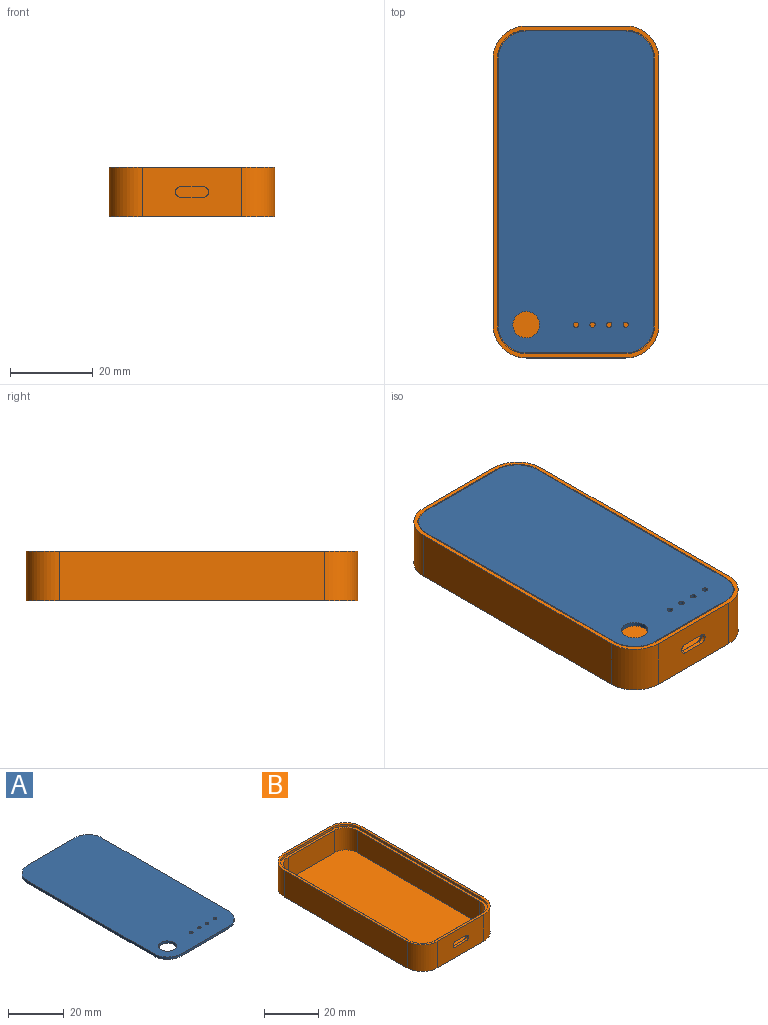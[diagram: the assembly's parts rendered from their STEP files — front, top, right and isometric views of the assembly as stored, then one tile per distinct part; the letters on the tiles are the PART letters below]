
ASSEMBLY  parts=2 mates=1
PART A: 15 faces, bbox 37.6x77.6x1 mm
  f0: plane 24x1mm, normal (0,-1,0), area 24mm2, adj f4,f5,f6,f9
  f1: plane 64x1mm, normal (1,0,0), area 64mm2, adj f4,f5,f6,f7
  f2: plane 24x1mm, normal (0,1,0), area 24mm2, adj f4,f5,f7,f8
  f3: plane 64x1mm, normal (-1,0,0), area 64mm2, adj f4,f5,f8,f9
  f4: plane 77.6x37.6mm, normal (0,0,1), area 2840.6mm2, adj f0,f1,f2,f3,f6,f7,f8,f9
  f5: plane 77.6x37.6mm, normal (0,0,-1), area 2840.6mm2, adj f0,f1,f2,f3,f6,f7,f8,f9
  f6: cylinder r=6.8mm len=6.8mm, axis (0,0,1), area 10.7mm2, adj f0,f1,f4,f5
  f7: cylinder r=6.8mm len=6.8mm, axis (0,0,-1), area 10.7mm2, adj f1,f2,f4,f5
  f8: cylinder r=6.8mm len=6.8mm, axis (0,0,1), area 10.7mm2, adj f2,f3,f4,f5
  f9: cylinder r=6.8mm len=6.8mm, axis (0,0,-1), area 10.7mm2, adj f0,f3,f4,f5
  f10: cylinder r=3.2mm len=6.4mm, axis (0,0,1), area 20.1mm2, adj f4,f5
  f11: cylinder r=0.65mm len=1.3mm, axis (0,0,1), area 4.1mm2, adj f4,f5
  f12: cylinder r=0.65mm len=1.3mm, axis (0,0,1), area 4.1mm2, adj f4,f5
  f13: cylinder r=0.65mm len=1.3mm, axis (0,0,1), area 4.1mm2, adj f4,f5
  f14: cylinder r=0.65mm len=1.3mm, axis (0,0,1), area 4.1mm2, adj f4,f5
PART B: 36 faces, bbox 40x80x12 mm
  f0: plane 80x40mm, normal (0,0,1), area 223.1mm2, adj f1,f2,f3,f4,f6,f7,f8,f9
  f1: plane 24x12mm, normal (0,-1,0), area 269.3mm2, adj f0,f5,f6,f9,f28,f29,f30,f31
  f2: plane 64x12mm, normal (1,0,0), area 768mm2, adj f0,f5,f6,f7
  f3: plane 24x12mm, normal (0,1,0), area 288mm2, adj f0,f5,f7,f8
  f4: plane 64x12mm, normal (-1,0,0), area 768mm2, adj f0,f5,f8,f9
  f5: plane 80x40mm, normal (0,0,-1), area 3145.1mm2, adj f1,f2,f3,f4,f6,f7,f8,f9
  f6: cylinder r=8mm len=12mm, axis (0,0,1), area 150.8mm2, adj f0,f1,f2,f5
  f7: cylinder r=8mm len=12mm, axis (0,0,-1), area 150.8mm2, adj f0,f2,f3,f5
  f8: cylinder r=8mm len=12mm, axis (0,0,1), area 150.8mm2, adj f0,f3,f4,f5
  f9: cylinder r=8mm len=12mm, axis (0,0,-1), area 150.8mm2, adj f0,f1,f4,f5
  f10: plane 24x1mm, normal (0,1,0), area 24mm2, adj f0,f14,f17,f26
  f11: plane 64x1mm, normal (-1,0,0), area 64mm2, adj f0,f14,f15,f26
  f12: plane 24x1mm, normal (0,-1,0), area 24mm2, adj f0,f15,f16,f26
  f13: plane 64x1mm, normal (1,0,0), area 64mm2, adj f0,f16,f17,f26
  f14: cylinder r=7mm len=7mm, axis (0,0,1), area 11mm2, adj f0,f10,f11,f26
  f15: cylinder r=7mm len=7mm, axis (0,0,-1), area 11mm2, adj f0,f11,f12,f26
  f16: cylinder r=7mm len=7mm, axis (0,0,1), area 11mm2, adj f0,f12,f13,f26
  f17: cylinder r=7mm len=7mm, axis (0,0,-1), area 11mm2, adj f0,f10,f13,f26
  f18: cylinder r=6mm len=10mm, axis (0,0,-1), area 94.2mm2, adj f19,f25,f26,f27
  f19: plane 24x10mm, normal (0,-1,0), area 240mm2, adj f18,f20,f26,f27
  f20: cylinder r=6mm len=10mm, axis (0,0,-1), area 94.2mm2, adj f19,f21,f26,f27
  f21: plane 64x10mm, normal (-1,0,0), area 640mm2, adj f20,f22,f26,f27
  f22: cylinder r=6mm len=10mm, axis (0,0,-1), area 94.2mm2, adj f21,f23,f26,f27
  f23: plane 24x10mm, normal (0,1,0), area 199.3mm2, adj f22,f24,f26,f27,f32,f33,f34,f35
  f24: cylinder r=6mm len=10mm, axis (0,0,-1), area 94.2mm2, adj f23,f25,f26,f27
  f25: plane 64x10mm, normal (1,0,0), area 640mm2, adj f18,f24,f26,f27
  f26: plane 78x38mm, normal (0,0,1), area 216.8mm2, adj f10,f11,f12,f13,f14,f15,f16,f17
  f27: plane 76x36mm, normal (0,0,1), area 2705.1mm2, adj f18,f19,f20,f21,f22,f23,f24,f25
  f28: cylinder r=1.25mm len=2.5mm, axis (0,-1,0), area 3.9mm2, adj f1,f29,f30,f34
  f29: plane 5.5x1mm, normal (0,0,-1), area 5.5mm2, adj f1,f28,f31,f32
  f30: plane 5.5x1mm, normal (0,0,1), area 5.5mm2, adj f1,f28,f31,f35
  f31: cylinder r=1.25mm len=2.5mm, axis (0,-1,0), area 3.9mm2, adj f1,f29,f30,f33
  f32: plane 5.5x1mm, normal (0,0.71,-0.71), area 7.8mm2, adj f23,f29,f33,f34
  f33: cone r=2.25mm half-angle=45deg, axis (0,1,0), area 7.8mm2, adj f23,f31,f32,f35
  f34: cone r=2.25mm half-angle=45deg, axis (0,1,0), area 7.8mm2, adj f23,f28,f32,f35
  f35: plane 5.5x1mm, normal (0,0.71,0.71), area 7.8mm2, adj f23,f30,f33,f34
PLACE A t=(0,0,11)mm
PLACE B at identity
MATE fastened B.f8 <-> A.f8  axis (0,0,1) through (-12,32,12)mm
